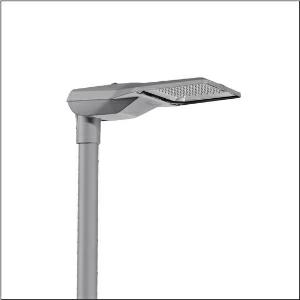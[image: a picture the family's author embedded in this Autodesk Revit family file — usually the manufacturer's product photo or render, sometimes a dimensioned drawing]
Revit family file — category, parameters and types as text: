
# Revit family: streetlight_sl_21_iq_midi___st1_0a_5xe3d31v08mb_ff90
name_source: partatom
category: Lighting Fixtures
units: mm (PartAtom-declared; Revit-internal decimal feet)

## family parameters
Cut with Voids When Loaded = No
Host = Face
Light Source = No
Part Type = Normal
Room Calculation Point = No
Round Connector Dimension = Use Diameter
Shared = No

## types (1)
- --- (1 x LED, 18340 lm, 129.3 W, 3000K)
    Apparent Load = 129 VA
    CIE Flux Codes = 37 72 97 100 100
    Color Rendering = 70
    Color Temperature = 3000K
    Default Elevation = 1800 mm
    Description = Streetlight SL 21 iQ midi, mast luminaire, primary light control with lens, of PMMA, primary optical cover: cover, of toughened safety glass, transparent, light distribution: ST1.0a, light emission: direct distribution, primary light characteristic: asymmetric, installation type: post-top, side-entry, LED, High Power LED, rated luminous flux: 18.340lm, luminous efficacy: 142lm/W, light colour: 730, colour temperature: 3000K, control: presetting dimming logarithmic, Street-Remote, Auto-Match, Temp-Guard, Lumen-Switch, Night-Set, Smart-Wire, Light-Fading, Desk-Remote (wireless, voltage-free reading and setting of iQ features in the workshop via application-optimized NFC function/RFID function), optimised constant luminous flux control (CLO 2.0), mains connection: 230..240V, AC, 50/60Hz, start of lifetime: 129W, end of service life: 142W, reduction: 56W, luminaire housing, of diecast aluminium, powder-coated, Siteco® metallic grey (DB 702S), corrosivity category C5 mid according to DIN EN ISO 12944, please order mast flange separately, inclination adjustable: 0°, 5°, 10°, 15°, sealing non-destructively replaceable, multi-level sealing system, length: 644mm, width: 335mm, height: 110mm, mast flange for spigot size: 42mm (side-entry): 5XC10008XM4, 60/48mm (side-entry/post-top): 5XC10108XM2, 76/60mm (side-entry/post-top): 5XC10108XM1, Smart Interface above, protection rating (complete): IP66, insulation class (complete): insulation class II (safety insulation), certification: CE, ENEC, ENEC+, VDE, impact resistance: IK09, permissible operating ambient temperature for outdoor applications: -40..+50°C, standard-compliant lighting for roads and squares, packaging unit: 1 piece

Light Distribution: ST1.0a
    Height = 111 mm
    Lamp = 1 x LED
    Lamp Light Flux = 18340 lm
    Lamp Power = 129.3 W
    Lamp count = 1
    Length = 644 mm
    Luminous efficacy = 142 lm/W
    Manufacturer = Siteco
    ModVariant = No
    Model = 5XE3D31V08MB
    Number of Poles = 1
    OnlyDefault = Yes
    Power Factor = 1
    Product Name = Streetlight SL 21 iQ midi | ST1.0a
    Product group = mast luminaire | pylon top
    ProductGroupID = 6100
    Protection Class = Protection class II
    Protection Degree = IP 66
    RLX_Detail_Level = 1
    RLX_Emergency_Light_Flux = 0 lm
    RLX_Emergency_Type = 0
    RLX_Emergency_Type_DB = No
    RlxData = <blob elided: 90889 chars, md5=853597c7>
    Socket = socket
    Standby Power = 0 W
    System Light Flux = 18340 lm
    System Power = 129 W
    Type Comments = factory setting: luminous flux: 100 % | dim-lin: 254 | 672 mA
    Type Image = l_1004302.jpg
    URL = http://relux.com
    VarID = @adj_062841
    Voltage = 0 V
    Weight = 0.00 kg
    Width = 336 mm

## geometry (parser evidence)
native form markers: Blend x4, Sweep x13
no freeform markers — native parametric forms only
